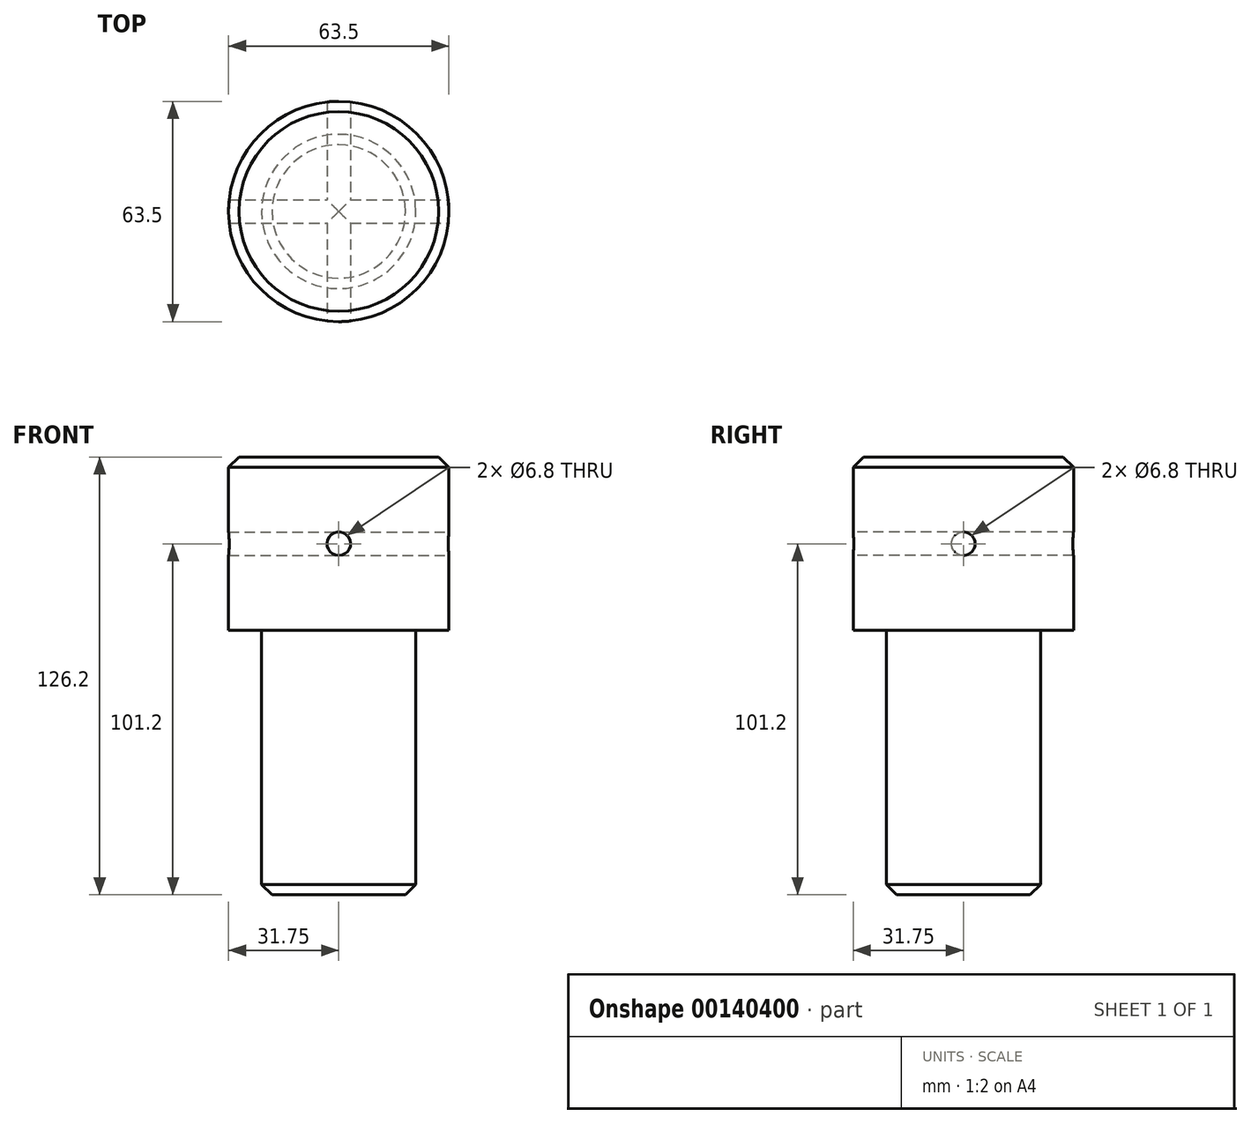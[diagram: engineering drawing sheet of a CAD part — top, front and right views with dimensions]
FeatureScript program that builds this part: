
annotation { "Feature Type Name" : "Feature", "Feature Type Description" : "" }
export const myFeature = defineFeature(function(context is Context, id is Id, definition is map)
    precondition{}
    {
        {
            var Q0;
            Q0=qCreatedBy(makeId("Top.planeOp"),FACE);
            var sketch = newSketch(context, id + "F0", { "sketchPlane" : qUnion([Q0])});
            skCircle(sketch, "E0", {"center": v(0, 0) * mm, "radius": 22.23 * mm});
            skCircle(sketch, "E1", {"center": v(0, 0) * mm, "radius": 31.75 * mm});
            skSolve(sketch);
        }
        {
            var Q0;
            Q0=makeQuery(id+"F0.imprint","IMPRINT",FACE,{"disambiguationData":[TD([[makeQuery(id+"F0.imprint","IMPRINT",EDGE,{"derivedFrom":sQuery(id+"F0.wireOp",EDGE,"E0")}),1.0]])]});
            extrude(context, id + "F1", {"entities" : qUnion([Q0]), "oppositeDirection" : true, "depth" : 76.2 * mm});
        }
        {
            var Q0;
            Q0=makeQuery(id+"F0.imprint","IMPRINT",FACE,{"disambiguationData":[TD([[makeQuery(id+"F0.imprint","IMPRINT",EDGE,{"derivedFrom":sQuery(id+"F0.wireOp",EDGE,"E0")}),-1.0]])]});
            var Q1;
            Q1=makeQuery(id+"F0.imprint","IMPRINT",FACE,{"disambiguationData":[TD([[makeQuery(id+"F0.imprint","IMPRINT",EDGE,{"derivedFrom":sQuery(id+"F0.wireOp",EDGE,"E0")}),1.0]])]});
            extrude(context, id + "F2", {"entities" : qUnion([Q0, Q1]), "operationType" : NewBodyOperationType.ADD, "depth" : 50 * mm});
        }
        {
            var Q0;
            Q0=makeQuery(id+"F2.opExtrude","CAP_EDGE",EDGE,{"disambiguationData":[OSD([sQuery(id+"F0.wireOp",EDGE,"E1")])],"isStart":false});
            var Q1;
            Q1=makeQuery(id+"F1.opExtrude","CAP_EDGE",EDGE,{"disambiguationData":[OSD([sQuery(id+"F0.wireOp",EDGE,"E0")])],"isStart":false});
            chamfer(context, id + "F3", {"entities" : qUnion([Q0, Q1]), "width" : 3 * mm, "tangentPropagation" : true});
        }
        {
            var Q0;
            Q0=makeQuery(id+"F2.opExtrude","CAP_FACE",FACE,{"disambiguationData":[OSD([sQuery(id+"F0.wireOp",EDGE,"E1")])],"isStart":false});
            var sketch = newSketch(context, id + "F4", { "sketchPlane" : qUnion([Q0])});
            skLineSegment(sketch, "E2", {"start": v(0, 28.75) * mm, "end": v(0, -31.75) * mm});
            skLineSegment(sketch, "E3", {"start": v(-28.75, 0) * mm, "end": v(31.75, 0) * mm});
            skPoint(sketch, "E4.orphan", {"position": v(-28.75, 0) * mm});
            skPoint(sketch, "E5.orphan", {"position": v(0, 28.75) * mm});
            skSolve(sketch);
        }
        {
            var Q0;
            Q0=qCreatedBy(makeId("Right.planeOp"),FACE);
            var Q1;
            Q1=sQuery(id+"F4.wireOp",VERTEX,"E3.end");
            cPlane(context, id + "F5", {"entities" : qUnion([Q0, Q1]), "cplaneType" : CPlaneType.PLANE_POINT, "offset" : 25 * mm, "width" : 150 * mm, "height" : 150 * mm});
        }
        {
            var Q0;
            Q0=qCreatedBy(makeId("Front.planeOp"),FACE);
            var Q1;
            Q1=sQuery(id+"F4.wireOp",VERTEX,"E2.end");
            cPlane(context, id + "F6", {"entities" : qUnion([Q0, Q1]), "cplaneType" : CPlaneType.PLANE_POINT, "offset" : 25 * mm, "width" : 150 * mm, "height" : 150 * mm});
        }
        {
            var Q0;
            Q0=qCreatedBy(id+"F5.planeOp",FACE);
            var sketch = newSketch(context, id + "F7", { "sketchPlane" : qUnion([Q0])});
            skPoint(sketch, "E6", {"position": v(0, 25) * mm});
            skSolve(sketch);
        }
        {
            var Q0;
            Q0=qCreatedBy(id+"F6.planeOp",FACE);
            var sketch = newSketch(context, id + "F8", { "sketchPlane" : qUnion([Q0])});
            skPoint(sketch, "E7", {"position": v(0, 25) * mm});
            skSolve(sketch);
        }
        {
            var Q0;
            Q0=sQuery(id+"F8.wireOp",VERTEX,"E7");
            var Q1;
            Q1=sQuery(id+"F7.wireOp",VERTEX,"E6");
            var Q2;
            Q2=makeQuery(id+"F1.opExtrude","SWEPT_BODY",BODY,{"disambiguationData":[OSD([sQuery(id+"F0.wireOp",EDGE,"E0")])]});
            hole(context, id + "F9", {"style" : HoleStyle.SIMPLE, "endStyle" : HoleEndStyle.THROUGH, "standardTappedOrClearance" : lookupTablePath({ "standard" : "ISO", "engagement" : "75%", "pitch" : "1.25 mm", "size" : "M8", "type" : "Tapped" }), "standardBlindInLast" : lookupTablePath({ "standard" : "ISO", "engagement" : "75%", "pitch" : "1.25 mm", "size" : "M8", "type" : "Tapped" }), "holeDiameter" : 6.8 * mm, "startFromSketch" : true, "locations" : qUnion([Q0, Q1]), "scope" : qUnion([Q2]), "isTappedThrough" : true, "majorDiameter" : 8 * mm, "showTappedDepth" : true});
        }
    });
